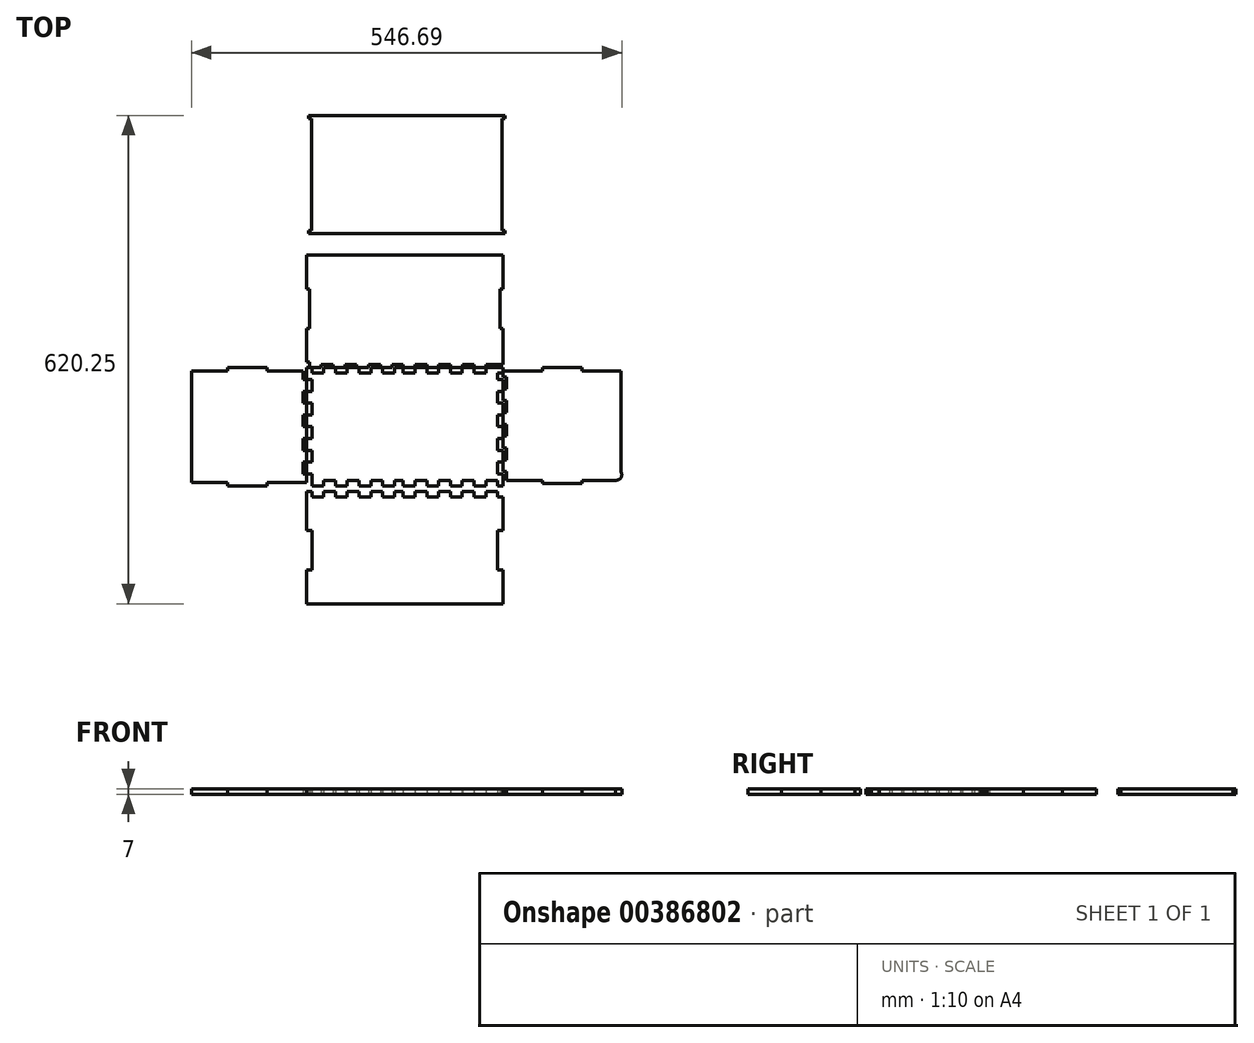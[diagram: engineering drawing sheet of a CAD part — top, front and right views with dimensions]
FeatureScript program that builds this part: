
annotation { "Feature Type Name" : "Feature", "Feature Type Description" : "" }
export const myFeature = defineFeature(function(context is Context, id is Id, definition is map)
    precondition{}
    {
        {
            var Q0;
            Q0=qCreatedBy(makeId("Top.planeOp"),FACE);
            var sketch = newSketch(context, id + "F0", { "sketchPlane" : qUnion([Q0])});
            skLineSegment(sketch, "E0.bottom", {"start": v(-116.1, -76.62) * mm, "end": v(-101.1, -76.62) * mm});
            skLineSegment(sketch, "E0.right", {"start": v(126.9, -76.62) * mm, "end": v(126.9, -61.62) * mm});
            skLineSegment(sketch, "E1.0", {"start": v(-123.1, -61.62) * mm, "end": v(-116.1, -61.62) * mm});
            skLineSegment(sketch, "E2.0", {"start": v(-123.1, -46.62) * mm, "end": v(-116.1, -46.62) * mm});
            skLineSegment(sketch, "E3.0", {"start": v(-123.1, -31.62) * mm, "end": v(-116.1, -31.62) * mm});
            skLineSegment(sketch, "E4.0", {"start": v(-123.1, -16.62) * mm, "end": v(-116.1, -16.62) * mm});
            skLineSegment(sketch, "E5.0", {"start": v(-123.1, -1.62) * mm, "end": v(-116.1, -1.62) * mm});
            skLineSegment(sketch, "E6.0", {"start": v(-123.1, 13.38) * mm, "end": v(-116.1, 13.38) * mm});
            skLineSegment(sketch, "E7.0", {"start": v(-123.1, 28.38) * mm, "end": v(-116.1, 28.38) * mm});
            skLineSegment(sketch, "E8.0", {"start": v(-123.1, 43.38) * mm, "end": v(-116.1, 43.38) * mm});
            skLineSegment(sketch, "E9.0", {"start": v(-123.1, 58.38) * mm, "end": v(-116.1, 58.38) * mm});
            skLineSegment(sketch, "E10.0", {"start": v(-116.1, 66.38) * mm, "end": v(-101.1, 66.38) * mm});
            skLineSegment(sketch, "E11.0", {"start": v(119.9, -76.62) * mm, "end": v(119.9, -69.62) * mm});
            skLineSegment(sketch, "E12.trimOffspring", {"start": v(119.9, 58.38) * mm, "end": v(126.9, 58.38) * mm});
            skLineSegment(sketch, "E13.trimOffspring", {"start": v(119.9, 43.38) * mm, "end": v(126.9, 43.38) * mm});
            skLineSegment(sketch, "E14.trimOffspring", {"start": v(119.9, 28.38) * mm, "end": v(126.9, 28.38) * mm});
            skLineSegment(sketch, "E15.trimOffspring", {"start": v(119.9, 13.38) * mm, "end": v(126.9, 13.38) * mm});
            skLineSegment(sketch, "E16.trimOffspring", {"start": v(119.9, -1.62) * mm, "end": v(126.9, -1.62) * mm});
            skLineSegment(sketch, "E17.trimOffspring", {"start": v(119.9, -16.62) * mm, "end": v(126.9, -16.62) * mm});
            skLineSegment(sketch, "E18.trimOffspring", {"start": v(119.9, -31.62) * mm, "end": v(126.9, -31.62) * mm});
            skLineSegment(sketch, "E19.trimOffspring", {"start": v(119.9, -61.62) * mm, "end": v(126.9, -61.62) * mm});
            skLineSegment(sketch, "E20.trimOffspring", {"start": v(119.9, -46.62) * mm, "end": v(126.9, -46.62) * mm});
            skLineSegment(sketch, "E21.trimOffspring", {"start": v(126.9, 66.38) * mm, "end": v(126.9, 73.38) * mm});
            skLineSegment(sketch, "E22.trimOffspring", {"start": v(126.9, 43.38) * mm, "end": v(126.9, 58.38) * mm});
            skLineSegment(sketch, "E23.trimOffspring", {"start": v(126.9, 13.38) * mm, "end": v(126.9, 28.38) * mm});
            skLineSegment(sketch, "E24.trimOffspring", {"start": v(126.9, -16.62) * mm, "end": v(126.9, -1.62) * mm});
            skLineSegment(sketch, "E25.trimOffspring", {"start": v(126.9, -46.62) * mm, "end": v(126.9, -31.62) * mm});
            skLineSegment(sketch, "E26.0", {"start": v(-101.1, 73.38) * mm, "end": v(-101.1, 66.38) * mm});
            skLineSegment(sketch, "E27.0", {"start": v(-86.1, 73.38) * mm, "end": v(-86.1, 66.38) * mm});
            skLineSegment(sketch, "E28.0", {"start": v(-71.1, 73.38) * mm, "end": v(-71.1, 66.38) * mm});
            skLineSegment(sketch, "E29.0", {"start": v(-56.1, 73.38) * mm, "end": v(-56.1, 66.38) * mm});
            skLineSegment(sketch, "E30.0", {"start": v(-41.1, 73.38) * mm, "end": v(-41.1, 66.38) * mm});
            skLineSegment(sketch, "E31.0", {"start": v(-26.1, 73.38) * mm, "end": v(-26.1, 66.38) * mm});
            skLineSegment(sketch, "E32.0", {"start": v(-11.1, 73.38) * mm, "end": v(-11.1, 66.38) * mm});
            skLineSegment(sketch, "E33.0", {"start": v(104.9, -76.62) * mm, "end": v(104.9, -69.62) * mm});
            skLineSegment(sketch, "E34.0", {"start": v(89.9, -76.62) * mm, "end": v(89.9, -69.62) * mm});
            skLineSegment(sketch, "E35.0", {"start": v(74.9, -76.62) * mm, "end": v(74.9, -69.62) * mm});
            skLineSegment(sketch, "E36.0", {"start": v(59.9, -76.62) * mm, "end": v(59.9, -69.62) * mm});
            skLineSegment(sketch, "E37.0", {"start": v(44.9, -76.62) * mm, "end": v(44.9, -69.62) * mm});
            skLineSegment(sketch, "E38.0", {"start": v(29.9, -76.62) * mm, "end": v(29.9, -69.62) * mm});
            skLineSegment(sketch, "E39.0", {"start": v(14.9, -76.62) * mm, "end": v(14.9, -69.62) * mm});
            skLineSegment(sketch, "E40.0", {"start": v(-0.1, -76.62) * mm, "end": v(-0.1, -69.62) * mm});
            skLineSegment(sketch, "E41.trimOffspring", {"start": v(-101.1, 73.38) * mm, "end": v(-86.1, 73.38) * mm});
            skLineSegment(sketch, "E42.trimOffspring", {"start": v(-86.1, -76.62) * mm, "end": v(-71.1, -76.62) * mm});
            skLineSegment(sketch, "E43.trimOffspring", {"start": v(-71.1, 73.38) * mm, "end": v(-56.1, 73.38) * mm});
            skLineSegment(sketch, "E44.trimOffspring", {"start": v(-56.1, -76.62) * mm, "end": v(-41.1, -76.62) * mm});
            skLineSegment(sketch, "E45.trimOffspring", {"start": v(-41.1, 73.38) * mm, "end": v(-26.1, 73.38) * mm});
            skLineSegment(sketch, "E46.trimOffspring", {"start": v(-11.1, 73.38) * mm, "end": v(-0.1, 73.38) * mm});
            skLineSegment(sketch, "E47.trimOffspring", {"start": v(14.9, 73.38) * mm, "end": v(29.9, 73.38) * mm});
            skLineSegment(sketch, "E48.trimOffspring", {"start": v(44.9, 73.38) * mm, "end": v(59.9, 73.38) * mm});
            skLineSegment(sketch, "E49.trimOffspring", {"start": v(74.9, 73.38) * mm, "end": v(89.9, 73.38) * mm});
            skLineSegment(sketch, "E50.trimOffspring", {"start": v(104.9, 73.38) * mm, "end": v(126.9, 73.38) * mm});
            skLineSegment(sketch, "E51.trimOffspring", {"start": v(119.9, -76.62) * mm, "end": v(126.9, -76.62) * mm});
            skLineSegment(sketch, "E52.trimOffspring", {"start": v(89.9, -76.62) * mm, "end": v(104.9, -76.62) * mm});
            skLineSegment(sketch, "E53.trimOffspring", {"start": v(59.9, -76.62) * mm, "end": v(74.9, -76.62) * mm});
            skLineSegment(sketch, "E54.trimOffspring", {"start": v(29.9, -76.62) * mm, "end": v(44.9, -76.62) * mm});
            skLineSegment(sketch, "E55.trimOffspring", {"start": v(-0.1, -76.62) * mm, "end": v(14.9, -76.62) * mm});
            skLineSegment(sketch, "E56.trimOffspring", {"start": v(-26.1, -76.62) * mm, "end": v(-11.1, -76.62) * mm});
            skLineSegment(sketch, "E57.trimOffspring", {"start": v(-86.1, 66.38) * mm, "end": v(-71.1, 66.38) * mm});
            skLineSegment(sketch, "E58.trimOffspring", {"start": v(-101.1, -69.62) * mm, "end": v(-101.1, -76.62) * mm});
            skLineSegment(sketch, "E59.trimOffspring", {"start": v(-86.1, -69.62) * mm, "end": v(-86.1, -76.62) * mm});
            skLineSegment(sketch, "E60.trimOffspring", {"start": v(-71.1, -69.62) * mm, "end": v(-71.1, -76.62) * mm});
            skLineSegment(sketch, "E61.trimOffspring", {"start": v(-56.1, -69.62) * mm, "end": v(-56.1, -76.62) * mm});
            skLineSegment(sketch, "E62.trimOffspring", {"start": v(-41.1, -69.62) * mm, "end": v(-41.1, -76.62) * mm});
            skLineSegment(sketch, "E63.trimOffspring", {"start": v(-26.1, -69.62) * mm, "end": v(-26.1, -76.62) * mm});
            skLineSegment(sketch, "E64.trimOffspring", {"start": v(-11.1, -69.62) * mm, "end": v(-11.1, -76.62) * mm});
            skLineSegment(sketch, "E65.trimOffspring", {"start": v(-0.1, 66.38) * mm, "end": v(-0.1, 73.38) * mm});
            skLineSegment(sketch, "E66.trimOffspring", {"start": v(14.9, 66.38) * mm, "end": v(14.9, 73.38) * mm});
            skLineSegment(sketch, "E67.trimOffspring", {"start": v(29.9, 66.38) * mm, "end": v(29.9, 73.38) * mm});
            skLineSegment(sketch, "E68.trimOffspring", {"start": v(44.9, 66.38) * mm, "end": v(44.9, 73.38) * mm});
            skLineSegment(sketch, "E69.trimOffspring", {"start": v(59.9, 66.38) * mm, "end": v(59.9, 73.38) * mm});
            skLineSegment(sketch, "E70.trimOffspring", {"start": v(74.9, 66.38) * mm, "end": v(74.9, 73.38) * mm});
            skLineSegment(sketch, "E71.trimOffspring", {"start": v(89.9, 66.38) * mm, "end": v(89.9, 73.38) * mm});
            skLineSegment(sketch, "E72.trimOffspring", {"start": v(104.9, 66.38) * mm, "end": v(104.9, 73.38) * mm});
            skLineSegment(sketch, "E73.trimOffspring", {"start": v(119.9, 66.38) * mm, "end": v(126.9, 66.38) * mm});
            skLineSegment(sketch, "E74.trimOffspring", {"start": v(119.9, 58.38) * mm, "end": v(119.9, 66.38) * mm});
            skLineSegment(sketch, "E75.trimOffspring", {"start": v(119.9, 28.38) * mm, "end": v(119.9, 43.38) * mm});
            skLineSegment(sketch, "E76.trimOffspring", {"start": v(119.9, -1.62) * mm, "end": v(119.9, 13.38) * mm});
            skLineSegment(sketch, "E77.trimOffspring", {"start": v(119.9, -31.62) * mm, "end": v(119.9, -16.62) * mm});
            skLineSegment(sketch, "E78.trimOffspring", {"start": v(119.9, -61.62) * mm, "end": v(119.9, -46.62) * mm});
            skLineSegment(sketch, "E79.trimOffspring", {"start": v(104.9, -69.62) * mm, "end": v(119.9, -69.62) * mm});
            skLineSegment(sketch, "E80.trimOffspring", {"start": v(74.9, -69.62) * mm, "end": v(89.9, -69.62) * mm});
            skLineSegment(sketch, "E81.trimOffspring", {"start": v(44.9, -69.62) * mm, "end": v(59.9, -69.62) * mm});
            skLineSegment(sketch, "E82.trimOffspring", {"start": v(14.9, -69.62) * mm, "end": v(29.9, -69.62) * mm});
            skLineSegment(sketch, "E83.trimOffspring", {"start": v(-41.1, -69.62) * mm, "end": v(-26.1, -69.62) * mm});
            skLineSegment(sketch, "E84.trimOffspring", {"start": v(-11.1, -69.62) * mm, "end": v(-0.1, -69.62) * mm});
            skLineSegment(sketch, "E85.trimOffspring", {"start": v(-71.1, -69.62) * mm, "end": v(-56.1, -69.62) * mm});
            skLineSegment(sketch, "E86.trimOffspring", {"start": v(-101.1, -69.62) * mm, "end": v(-86.1, -69.62) * mm});
            skLineSegment(sketch, "E87.trimOffspring", {"start": v(-116.1, -16.62) * mm, "end": v(-116.1, -1.62) * mm});
            skLineSegment(sketch, "E88", {"start": v(-123.1, 43.38) * mm, "end": v(-123.1, 28.38) * mm});
            skLineSegment(sketch, "E89", {"start": v(-123.1, 13.38) * mm, "end": v(-123.1, -1.62) * mm});
            skLineSegment(sketch, "E90", {"start": v(-123.1, -16.62) * mm, "end": v(-123.1, -31.62) * mm});
            skLineSegment(sketch, "E91", {"start": v(-123.1, -46.62) * mm, "end": v(-123.1, -61.62) * mm});
            skLineSegment(sketch, "E92", {"start": v(-116.1, -61.62) * mm, "end": v(-116.1, -76.62) * mm});
            skLineSegment(sketch, "E93.trimOffspring", {"start": v(-116.1, 66.38) * mm, "end": v(-116.1, 73.38) * mm});
            skLineSegment(sketch, "E94.trimOffspring", {"start": v(-116.1, 58.38) * mm, "end": v(-116.1, 43.38) * mm});
            skLineSegment(sketch, "E95.trimOffspring", {"start": v(-56.1, 66.38) * mm, "end": v(-41.1, 66.38) * mm});
            skLineSegment(sketch, "E96.trimOffspring", {"start": v(-26.1, 66.38) * mm, "end": v(-11.1, 66.38) * mm});
            skLineSegment(sketch, "E97.trimOffspring", {"start": v(-0.1, 66.38) * mm, "end": v(14.9, 66.38) * mm});
            skLineSegment(sketch, "E98.trimOffspring", {"start": v(59.9, 66.38) * mm, "end": v(74.9, 66.38) * mm});
            skLineSegment(sketch, "E99.trimOffspring", {"start": v(89.9, 66.38) * mm, "end": v(104.9, 66.38) * mm});
            skLineSegment(sketch, "E100", {"start": v(29.9, 66.38) * mm, "end": v(44.9, 66.38) * mm});
            skLineSegment(sketch, "E101.trimOffspring", {"start": v(-116.1, 28.38) * mm, "end": v(-116.1, 13.38) * mm});
            skLineSegment(sketch, "E102.trimOffspring", {"start": v(-116.1, -1.62) * mm, "end": v(-116.1, -16.62) * mm});
            skLineSegment(sketch, "E103.trimOffspring", {"start": v(-116.1, 13.38) * mm, "end": v(-116.1, 28.38) * mm});
            skLineSegment(sketch, "E104.trimOffspring", {"start": v(-116.1, -31.62) * mm, "end": v(-116.1, -46.62) * mm});
            skLineSegment(sketch, "E105", {"start": v(-123.1, 73.38) * mm, "end": v(-123.1, 58.38) * mm});
            skLineSegment(sketch, "E106", {"start": v(-123.1, 73.38) * mm, "end": v(-116.1, 73.38) * mm});
            skSolve(sketch);
        }
        {
            var Q0;
            Q0=qCreatedBy(makeId("Top.planeOp"),FACE);
            var sketch = newSketch(context, id + "F1", { "sketchPlane" : qUnion([Q0])});
            skLineSegment(sketch, "E107.left", {"start": v(126.9, 69.38) * mm, "end": v(126.9, 61.38) * mm});
            skLineSegment(sketch, "E108.0", {"start": v(126.9, 61.38) * mm, "end": v(130.9, 61.38) * mm});
            skLineSegment(sketch, "E109.0", {"start": v(126.9, 46.38) * mm, "end": v(130.9, 46.38) * mm});
            skLineSegment(sketch, "E110.0", {"start": v(126.9, 31.38) * mm, "end": v(130.9, 31.38) * mm});
            skLineSegment(sketch, "E111.0", {"start": v(126.9, 16.38) * mm, "end": v(130.9, 16.38) * mm});
            skLineSegment(sketch, "E112.0", {"start": v(126.9, 1.38) * mm, "end": v(130.9, 1.38) * mm});
            skLineSegment(sketch, "E113.0", {"start": v(126.9, -13.62) * mm, "end": v(130.9, -13.62) * mm});
            skLineSegment(sketch, "E114.0", {"start": v(126.9, -28.62) * mm, "end": v(130.9, -28.62) * mm});
            skLineSegment(sketch, "E115.0", {"start": v(126.9, -43.62) * mm, "end": v(130.9, -43.62) * mm});
            skLineSegment(sketch, "E116.0", {"start": v(126.9, -58.62) * mm, "end": v(130.9, -58.62) * mm});
            skLineSegment(sketch, "E117.trimOffspring", {"start": v(126.9, 46.38) * mm, "end": v(126.9, 31.38) * mm});
            skLineSegment(sketch, "E118.trimOffspring", {"start": v(130.9, 61.38) * mm, "end": v(130.9, 46.38) * mm});
            skLineSegment(sketch, "E119.trimOffspring", {"start": v(126.9, 16.38) * mm, "end": v(126.9, 1.38) * mm});
            skLineSegment(sketch, "E120.trimOffspring", {"start": v(126.9, -13.62) * mm, "end": v(126.9, -28.62) * mm});
            skLineSegment(sketch, "E121.trimOffspring", {"start": v(126.9, -43.62) * mm, "end": v(126.9, -58.62) * mm});
            skLineSegment(sketch, "E122.trimOffspring", {"start": v(130.9, -58.62) * mm, "end": v(130.9, -69.62) * mm});
            skLineSegment(sketch, "E123.trimOffspring", {"start": v(130.9, -28.62) * mm, "end": v(130.9, -43.62) * mm});
            skLineSegment(sketch, "E124.trimOffspring", {"start": v(130.9, 1.38) * mm, "end": v(130.9, -13.62) * mm});
            skLineSegment(sketch, "E125.trimOffspring", {"start": v(130.9, 31.38) * mm, "end": v(130.9, 16.38) * mm});
            skLineSegment(sketch, "E126.0", {"start": v(130.9, -69.62) * mm, "end": v(176.9, -69.62) * mm});
            skLineSegment(sketch, "E127", {"start": v(176.9, -69.62) * mm, "end": v(176.9, -73.62) * mm});
            skLineSegment(sketch, "E128", {"start": v(176.9, -73.62) * mm, "end": v(226.9, -73.62) * mm});
            skLineSegment(sketch, "E129", {"start": v(226.9, -73.62) * mm, "end": v(226.9, -69.62) * mm});
            skLineSegment(sketch, "E130", {"start": v(176.9, 69.38) * mm, "end": v(176.9, 73.38) * mm});
            skLineSegment(sketch, "E131", {"start": v(176.9, 73.38) * mm, "end": v(226.9, 73.38) * mm});
            skLineSegment(sketch, "E132", {"start": v(226.9, 73.38) * mm, "end": v(226.9, 69.38) * mm});
            skLineSegment(sketch, "E133", {"start": v(226.9, 69.38) * mm, "end": v(276.9, 69.38) * mm});
            skLineSegment(sketch, "E134", {"start": v(226.9, -69.62) * mm, "end": v(269.9, -69.62) * mm});
            skLineSegment(sketch, "E135", {"start": v(126.9, 69.38) * mm, "end": v(176.9, 69.38) * mm});
            skLineSegment(sketch, "E136", {"start": v(276.9, 69.38) * mm, "end": v(276.9, -59.62) * mm});
            skArc(sketch, "E137", {"start": v(269.9, -69.62) * mm, "mid": v(276.32, -66.67) * mm, "end": v(276.9, -59.62) * mm});
            skSolve(sketch);
        }
        {
            var Q0;
            Q0=qCreatedBy(makeId("Top.planeOp"),FACE);
            var sketch = newSketch(context, id + "F2", { "sketchPlane" : qUnion([Q0])});
            skLineSegment(sketch, "E138.trimOffspring", {"start": v(-127.1, 58.38) * mm, "end": v(-123.1, 58.38) * mm});
            skLineSegment(sketch, "E139.trimOffspring", {"start": v(-127.1, 43.38) * mm, "end": v(-123.1, 43.38) * mm});
            skLineSegment(sketch, "E140.trimOffspring", {"start": v(-127.1, 28.38) * mm, "end": v(-123.1, 28.38) * mm});
            skLineSegment(sketch, "E141.trimOffspring", {"start": v(-127.1, 13.38) * mm, "end": v(-123.1, 13.38) * mm});
            skLineSegment(sketch, "E142.trimOffspring", {"start": v(-127.1, -1.62) * mm, "end": v(-123.1, -1.62) * mm});
            skLineSegment(sketch, "E143.trimOffspring", {"start": v(-127.1, -16.62) * mm, "end": v(-123.1, -16.62) * mm});
            skLineSegment(sketch, "E144.trimOffspring", {"start": v(-127.1, -31.62) * mm, "end": v(-123.1, -31.62) * mm});
            skLineSegment(sketch, "E145.trimOffspring", {"start": v(-127.1, -46.62) * mm, "end": v(-123.1, -46.62) * mm});
            skLineSegment(sketch, "E146.trimOffspring", {"start": v(-127.1, -61.62) * mm, "end": v(-123.1, -61.62) * mm});
            skLineSegment(sketch, "E147", {"start": v(-123.1, 58.38) * mm, "end": v(-123.1, 43.38) * mm});
            skLineSegment(sketch, "E148", {"start": v(-127.1, 43.38) * mm, "end": v(-127.1, 28.38) * mm});
            skLineSegment(sketch, "E149", {"start": v(-123.1, 28.38) * mm, "end": v(-123.1, 13.38) * mm});
            skLineSegment(sketch, "E150", {"start": v(-127.1, 13.38) * mm, "end": v(-127.1, -1.62) * mm});
            skLineSegment(sketch, "E151", {"start": v(-123.1, -1.62) * mm, "end": v(-123.1, -16.62) * mm});
            skLineSegment(sketch, "E152", {"start": v(-127.1, -16.62) * mm, "end": v(-127.1, -31.62) * mm});
            skLineSegment(sketch, "E153", {"start": v(-123.1, -31.62) * mm, "end": v(-123.1, -46.62) * mm});
            skLineSegment(sketch, "E154", {"start": v(-127.1, -46.62) * mm, "end": v(-127.1, -61.62) * mm});
            skLineSegment(sketch, "E155", {"start": v(-123.1, -61.62) * mm, "end": v(-123.1, -72.62) * mm});
            skLineSegment(sketch, "E156.0", {"start": v(-173.1, 69.38) * mm, "end": v(-127.1, 69.38) * mm});
            skLineSegment(sketch, "E157", {"start": v(-173.1, -72.62) * mm, "end": v(-123.1, -72.62) * mm});
            skLineSegment(sketch, "E158", {"start": v(-173.1, -72.62) * mm, "end": v(-173.1, -76.62) * mm});
            skLineSegment(sketch, "E159", {"start": v(-173.1, -76.62) * mm, "end": v(-223.1, -76.62) * mm});
            skLineSegment(sketch, "E160", {"start": v(-269.1, 69.38) * mm, "end": v(-223.1, 69.38) * mm});
            skLineSegment(sketch, "E161", {"start": v(-223.1, 69.38) * mm, "end": v(-223.1, 73.38) * mm});
            skLineSegment(sketch, "E162", {"start": v(-223.1, 73.38) * mm, "end": v(-173.1, 73.38) * mm});
            skLineSegment(sketch, "E163", {"start": v(-173.1, 73.38) * mm, "end": v(-173.1, 69.38) * mm});
            skLineSegment(sketch, "E164", {"start": v(-127.1, 58.38) * mm, "end": v(-127.1, 69.38) * mm});
            skLineSegment(sketch, "E165", {"start": v(-223.1, -76.62) * mm, "end": v(-223.1, -72.62) * mm});
            skLineSegment(sketch, "E166", {"start": v(-223.1, -72.62) * mm, "end": v(-269.1, -72.62) * mm});
            skLineSegment(sketch, "E167", {"start": v(-269.1, 69.38) * mm, "end": v(-269.1, -72.62) * mm});
            skSolve(sketch);
        }
        {
            var Q0;
            Q0=qCreatedBy(makeId("Top.planeOp"),FACE);
            var sketch = newSketch(context, id + "F3", { "sketchPlane" : qUnion([Q0])});
            skLineSegment(sketch, "E168.trimOffspring", {"start": v(-101.1, -83.62) * mm, "end": v(-86.1, -83.62) * mm});
            skLineSegment(sketch, "E169.trimOffspring", {"start": v(-71.1, -83.62) * mm, "end": v(-56.1, -83.62) * mm});
            skLineSegment(sketch, "E170", {"start": v(-41.1, -83.62) * mm, "end": v(-26.1, -83.62) * mm});
            skLineSegment(sketch, "E171", {"start": v(-101.1, -83.62) * mm, "end": v(-101.1, -90.62) * mm});
            skLineSegment(sketch, "E172", {"start": v(-123.1, -133.62) * mm, "end": v(-116.1, -133.62) * mm});
            skLineSegment(sketch, "E173", {"start": v(-116.1, -133.62) * mm, "end": v(-116.1, -183.62) * mm});
            skLineSegment(sketch, "E174", {"start": v(-116.1, -183.62) * mm, "end": v(-123.1, -183.62) * mm});
            skLineSegment(sketch, "E175", {"start": v(-123.1, -183.62) * mm, "end": v(-123.1, -226.62) * mm});
            skLineSegment(sketch, "E176", {"start": v(-123.1, -226.62) * mm, "end": v(126.9, -226.62) * mm});
            skLineSegment(sketch, "E177", {"start": v(126.9, -226.62) * mm, "end": v(126.9, -183.62) * mm});
            skLineSegment(sketch, "E178", {"start": v(119.9, -133.62) * mm, "end": v(126.9, -133.62) * mm});
            skLineSegment(sketch, "E179", {"start": v(119.9, -183.62) * mm, "end": v(126.9, -183.62) * mm});
            skLineSegment(sketch, "E180.0", {"start": v(119.9, -133.62) * mm, "end": v(119.9, -183.62) * mm});
            skLineSegment(sketch, "E181", {"start": v(-86.1, -83.62) * mm, "end": v(-86.1, -90.62) * mm});
            skLineSegment(sketch, "E182", {"start": v(-86.1, -90.62) * mm, "end": v(-71.1, -90.62) * mm});
            skLineSegment(sketch, "E183", {"start": v(-71.1, -90.62) * mm, "end": v(-71.1, -83.62) * mm});
            skLineSegment(sketch, "E184", {"start": v(-56.1, -83.62) * mm, "end": v(-56.1, -90.62) * mm});
            skLineSegment(sketch, "E185", {"start": v(-56.1, -90.62) * mm, "end": v(-41.1, -90.62) * mm});
            skLineSegment(sketch, "E186", {"start": v(-41.1, -90.62) * mm, "end": v(-41.1, -83.62) * mm});
            skLineSegment(sketch, "E187", {"start": v(-116.1, -83.62) * mm, "end": v(-123.1, -83.62) * mm});
            skLineSegment(sketch, "E188", {"start": v(-116.1, -83.62) * mm, "end": v(-116.1, -90.62) * mm});
            skLineSegment(sketch, "E189", {"start": v(-116.1, -90.62) * mm, "end": v(-101.1, -90.62) * mm});
            skLineSegment(sketch, "E190", {"start": v(-123.1, -83.62) * mm, "end": v(-123.1, -133.62) * mm});
            skLineSegment(sketch, "E191", {"start": v(-26.1, -83.62) * mm, "end": v(-26.1, -90.62) * mm});
            skLineSegment(sketch, "E192", {"start": v(-26.1, -90.62) * mm, "end": v(-11.1, -90.62) * mm});
            skLineSegment(sketch, "E193", {"start": v(-11.1, -90.62) * mm, "end": v(-11.1, -83.62) * mm});
            skLineSegment(sketch, "E194", {"start": v(-11.1, -83.62) * mm, "end": v(-0.1, -83.62) * mm});
            skLineSegment(sketch, "E195", {"start": v(-0.1, -83.62) * mm, "end": v(-0.1, -90.62) * mm});
            skLineSegment(sketch, "E196", {"start": v(119.9, -83.62) * mm, "end": v(119.9, -90.62) * mm});
            skLineSegment(sketch, "E197", {"start": v(104.9, -90.62) * mm, "end": v(104.9, -83.62) * mm});
            skLineSegment(sketch, "E198", {"start": v(-0.1, -90.62) * mm, "end": v(14.9, -90.62) * mm});
            skLineSegment(sketch, "E199", {"start": v(14.9, -90.62) * mm, "end": v(14.9, -83.62) * mm});
            skLineSegment(sketch, "E200", {"start": v(14.9, -83.62) * mm, "end": v(29.9, -83.62) * mm});
            skLineSegment(sketch, "E201", {"start": v(29.9, -83.62) * mm, "end": v(29.9, -90.62) * mm});
            skLineSegment(sketch, "E202", {"start": v(29.9, -90.62) * mm, "end": v(44.9, -90.62) * mm});
            skLineSegment(sketch, "E203", {"start": v(44.9, -90.62) * mm, "end": v(44.9, -83.62) * mm});
            skLineSegment(sketch, "E204", {"start": v(44.9, -83.62) * mm, "end": v(59.9, -83.62) * mm});
            skLineSegment(sketch, "E205", {"start": v(59.9, -83.62) * mm, "end": v(59.9, -90.62) * mm});
            skLineSegment(sketch, "E206", {"start": v(59.9, -90.62) * mm, "end": v(74.9, -90.62) * mm});
            skLineSegment(sketch, "E207", {"start": v(74.9, -90.62) * mm, "end": v(74.9, -83.62) * mm});
            skLineSegment(sketch, "E208", {"start": v(74.9, -83.62) * mm, "end": v(89.9, -83.62) * mm});
            skLineSegment(sketch, "E209", {"start": v(89.9, -83.62) * mm, "end": v(89.9, -90.62) * mm});
            skLineSegment(sketch, "E210", {"start": v(89.9, -90.62) * mm, "end": v(104.9, -90.62) * mm});
            skLineSegment(sketch, "E211", {"start": v(104.9, -83.62) * mm, "end": v(119.9, -83.62) * mm});
            skLineSegment(sketch, "E212", {"start": v(119.9, -90.62) * mm, "end": v(126.9, -90.62) * mm});
            skLineSegment(sketch, "E213", {"start": v(126.9, -90.62) * mm, "end": v(126.9, -133.62) * mm});
            skSolve(sketch);
        }
        {
            var Q0;
            Q0=makeQuery(id+"F0.imprint","IMPRINT",FACE,{"disambiguationData":[TD([[makeQuery(id+"F0.imprint","IMPRINT",EDGE,{"derivedFrom":sQuery(id+"F0.wireOp",EDGE,"E0.bottom")}),1.0]])]});
            extrude(context, id + "F4", {"entities" : qUnion([Q0]), "depth" : 7 * mm});
        }
        {
            var Q0;
            Q0=qCreatedBy(makeId("Top.planeOp"),FACE);
            var sketch = newSketch(context, id + "F5", { "sketchPlane" : qUnion([Q0])});
            skLineSegment(sketch, "E214.bottom", {"start": v(-119.1, 73.38) * mm, "end": v(-104.1, 73.38) * mm});
            skLineSegment(sketch, "E214.top", {"start": v(-123.1, 216.38) * mm, "end": v(126.9, 216.38) * mm});
            skLineSegment(sketch, "E214.left", {"start": v(-123.1, 80.38) * mm, "end": v(-123.1, 123.38) * mm});
            skLineSegment(sketch, "E214.right", {"start": v(126.9, 77.38) * mm, "end": v(126.9, 123.38) * mm});
            skLineSegment(sketch, "E215", {"start": v(-123.1, 80.38) * mm, "end": v(-119.1, 80.38) * mm});
            skLineSegment(sketch, "E216", {"start": v(-119.1, 80.38) * mm, "end": v(-119.1, 73.38) * mm});
            skLineSegment(sketch, "E217", {"start": v(-104.1, 73.38) * mm, "end": v(-104.1, 77.38) * mm});
            skLineSegment(sketch, "E218", {"start": v(-104.1, 77.38) * mm, "end": v(-89.1, 77.38) * mm});
            skLineSegment(sketch, "E219", {"start": v(-89.1, 77.38) * mm, "end": v(-89.1, 73.38) * mm});
            skLineSegment(sketch, "E220", {"start": v(-89.1, 73.38) * mm, "end": v(-74.1, 73.38) * mm});
            skLineSegment(sketch, "E221", {"start": v(-74.1, 73.38) * mm, "end": v(-74.1, 77.38) * mm});
            skLineSegment(sketch, "E222", {"start": v(-74.1, 77.38) * mm, "end": v(-59.1, 77.38) * mm});
            skLineSegment(sketch, "E223", {"start": v(-59.1, 77.38) * mm, "end": v(-59.1, 73.38) * mm});
            skLineSegment(sketch, "E224", {"start": v(-59.1, 73.38) * mm, "end": v(-44.1, 73.38) * mm});
            skLineSegment(sketch, "E225", {"start": v(-44.1, 73.38) * mm, "end": v(-44.1, 77.38) * mm});
            skLineSegment(sketch, "E226", {"start": v(-44.1, 77.38) * mm, "end": v(-29.1, 77.38) * mm});
            skLineSegment(sketch, "E227", {"start": v(-29.1, 77.38) * mm, "end": v(-29.1, 73.38) * mm});
            skLineSegment(sketch, "E228", {"start": v(-29.1, 73.38) * mm, "end": v(-14.1, 73.38) * mm});
            skLineSegment(sketch, "E229", {"start": v(-14.1, 73.38) * mm, "end": v(-14.1, 77.38) * mm});
            skLineSegment(sketch, "E230", {"start": v(-14.1, 77.38) * mm, "end": v(0, 77.38) * mm});
            skLineSegment(sketch, "E231", {"start": v(0, 77.38) * mm, "end": v(0, 73.38) * mm});
            skLineSegment(sketch, "E232", {"start": v(0, 73.38) * mm, "end": v(15, 73.38) * mm});
            skLineSegment(sketch, "E233", {"start": v(15, 73.38) * mm, "end": v(15, 77.38) * mm});
            skLineSegment(sketch, "E234", {"start": v(15, 77.38) * mm, "end": v(30, 77.38) * mm});
            skLineSegment(sketch, "E235", {"start": v(30, 77.38) * mm, "end": v(30, 73.38) * mm});
            skLineSegment(sketch, "E236", {"start": v(30, 73.38) * mm, "end": v(45, 73.38) * mm});
            skLineSegment(sketch, "E237", {"start": v(45, 73.38) * mm, "end": v(45, 77.38) * mm});
            skLineSegment(sketch, "E238", {"start": v(45, 77.38) * mm, "end": v(60, 77.38) * mm});
            skLineSegment(sketch, "E239", {"start": v(60, 77.38) * mm, "end": v(60, 73.38) * mm});
            skLineSegment(sketch, "E240", {"start": v(60, 73.38) * mm, "end": v(75, 73.38) * mm});
            skLineSegment(sketch, "E241", {"start": v(75, 73.38) * mm, "end": v(75, 77.38) * mm});
            skLineSegment(sketch, "E242", {"start": v(75, 77.38) * mm, "end": v(90, 77.38) * mm});
            skLineSegment(sketch, "E243", {"start": v(90, 77.38) * mm, "end": v(90, 73.38) * mm});
            skLineSegment(sketch, "E244", {"start": v(90, 73.38) * mm, "end": v(105, 73.38) * mm});
            skLineSegment(sketch, "E245", {"start": v(105, 73.38) * mm, "end": v(105, 77.38) * mm});
            skLineSegment(sketch, "E246", {"start": v(105, 77.38) * mm, "end": v(126.9, 77.38) * mm});
            skLineSegment(sketch, "E247.0", {"start": v(-123.1, 173.38) * mm, "end": v(-119.1, 173.38) * mm});
            skLineSegment(sketch, "E248.0", {"start": v(-123.1, 123.38) * mm, "end": v(-119.1, 123.38) * mm});
            skLineSegment(sketch, "E249.0", {"start": v(-119.1, 123.38) * mm, "end": v(-119.1, 173.38) * mm});
            skLineSegment(sketch, "E250.trimOffspring", {"start": v(-123.1, 173.38) * mm, "end": v(-123.1, 216.38) * mm});
            skLineSegment(sketch, "E251.trimOffspring", {"start": v(126.9, 173.38) * mm, "end": v(126.9, 216.38) * mm});
            skLineSegment(sketch, "E252.trimOffspring", {"start": v(122.9, 123.38) * mm, "end": v(122.9, 173.38) * mm});
            skLineSegment(sketch, "E253.trimOffspring", {"start": v(122.9, 123.38) * mm, "end": v(126.9, 123.38) * mm});
            skLineSegment(sketch, "E254.trimOffspring", {"start": v(122.9, 173.38) * mm, "end": v(126.9, 173.38) * mm});
            skPoint(sketch, "E255.orphan", {"position": v(126.9, 73.38) * mm});
            skSolve(sketch);
        }
        {
            var Q0;
            {var subQ1=sQuery(id+"F5.wireOp",EDGE,"E214.top");Q0=makeQuery(id+"F5.imprint","IMPRINT",FACE,{"disambiguationData":[TD([[makeQuery(id+"F5.imprint","IMPRINT",EDGE,{"derivedFrom":subQ1}),-1.0]])]});}
            extrude(context, id + "F6", {"entities" : qUnion([Q0]), "depth" : 7 * mm});
        }
        {
            var Q0;
            Q0=qCreatedBy(makeId("Top.planeOp"),FACE);
            var sketch = newSketch(context, id + "F7", { "sketchPlane" : qUnion([Q0])});
            skLineSegment(sketch, "E256.bottom", {"start": v(-120.46, 243.63) * mm, "end": v(129.54, 243.63) * mm});
            skLineSegment(sketch, "E256.top", {"start": v(-120.46, 393.63) * mm, "end": v(129.54, 393.63) * mm});
            skLineSegment(sketch, "E256.left", {"start": v(-120.46, 243.63) * mm, "end": v(-120.46, 247.63) * mm});
            skLineSegment(sketch, "E256.right", {"start": v(129.54, 243.63) * mm, "end": v(129.54, 247.63) * mm});
            skLineSegment(sketch, "E257.0", {"start": v(-120.46, 247.63) * mm, "end": v(-116.46, 247.63) * mm});
            skLineSegment(sketch, "E258.0", {"start": v(-120.46, 389.63) * mm, "end": v(-116.46, 389.63) * mm});
            skLineSegment(sketch, "E259.0", {"start": v(-116.46, 247.63) * mm, "end": v(-116.46, 389.63) * mm});
            skLineSegment(sketch, "E260.0", {"start": v(125.54, 247.63) * mm, "end": v(125.54, 389.63) * mm});
            skLineSegment(sketch, "E261.trimOffspring", {"start": v(-120.46, 389.63) * mm, "end": v(-120.46, 393.63) * mm});
            skLineSegment(sketch, "E262.trimOffspring", {"start": v(129.54, 389.63) * mm, "end": v(129.54, 393.63) * mm});
            skLineSegment(sketch, "E263.trimOffspring", {"start": v(125.54, 247.63) * mm, "end": v(129.54, 247.63) * mm});
            skLineSegment(sketch, "E264.trimOffspring", {"start": v(125.54, 389.63) * mm, "end": v(129.54, 389.63) * mm});
            skSolve(sketch);
        }
        {
            var Q0;
            Q0=makeQuery(id+"F2.imprint","IMPRINT",FACE,{"disambiguationData":[TD([[makeQuery(id+"F2.imprint","IMPRINT",EDGE,{"derivedFrom":sQuery(id+"F2.wireOp",EDGE,"E138.trimOffspring")}),-1.0]])]});
            extrude(context, id + "F8", {"entities" : qUnion([Q0]), "depth" : 7 * mm});
        }
        {
            var Q0;
            Q0=makeQuery(id+"F1.imprint","IMPRINT",FACE,{"disambiguationData":[TD([[makeQuery(id+"F1.imprint","IMPRINT",EDGE,{"derivedFrom":sQuery(id+"F1.wireOp",EDGE,"E107.left")}),1.0]])]});
            extrude(context, id + "F9", {"entities" : qUnion([Q0]), "depth" : 7 * mm});
        }
        {
            var Q0;
            Q0=makeQuery(id+"F7.imprint","IMPRINT",FACE,{"disambiguationData":[TD([[makeQuery(id+"F7.imprint","IMPRINT",EDGE,{"derivedFrom":sQuery(id+"F7.wireOp",EDGE,"E256.bottom")}),1.0]])]});
            extrude(context, id + "F10", {"entities" : qUnion([Q0]), "depth" : 7 * mm});
        }
        {
            var Q0;
            Q0=makeQuery(id+"F3.imprint","IMPRINT",FACE,{"disambiguationData":[TD([[makeQuery(id+"F3.imprint","IMPRINT",EDGE,{"derivedFrom":sQuery(id+"F3.wireOp",EDGE,"E168.trimOffspring")}),-1.0]])]});
            extrude(context, id + "F11", {"entities" : qUnion([Q0]), "depth" : 7 * mm});
        }
    });
